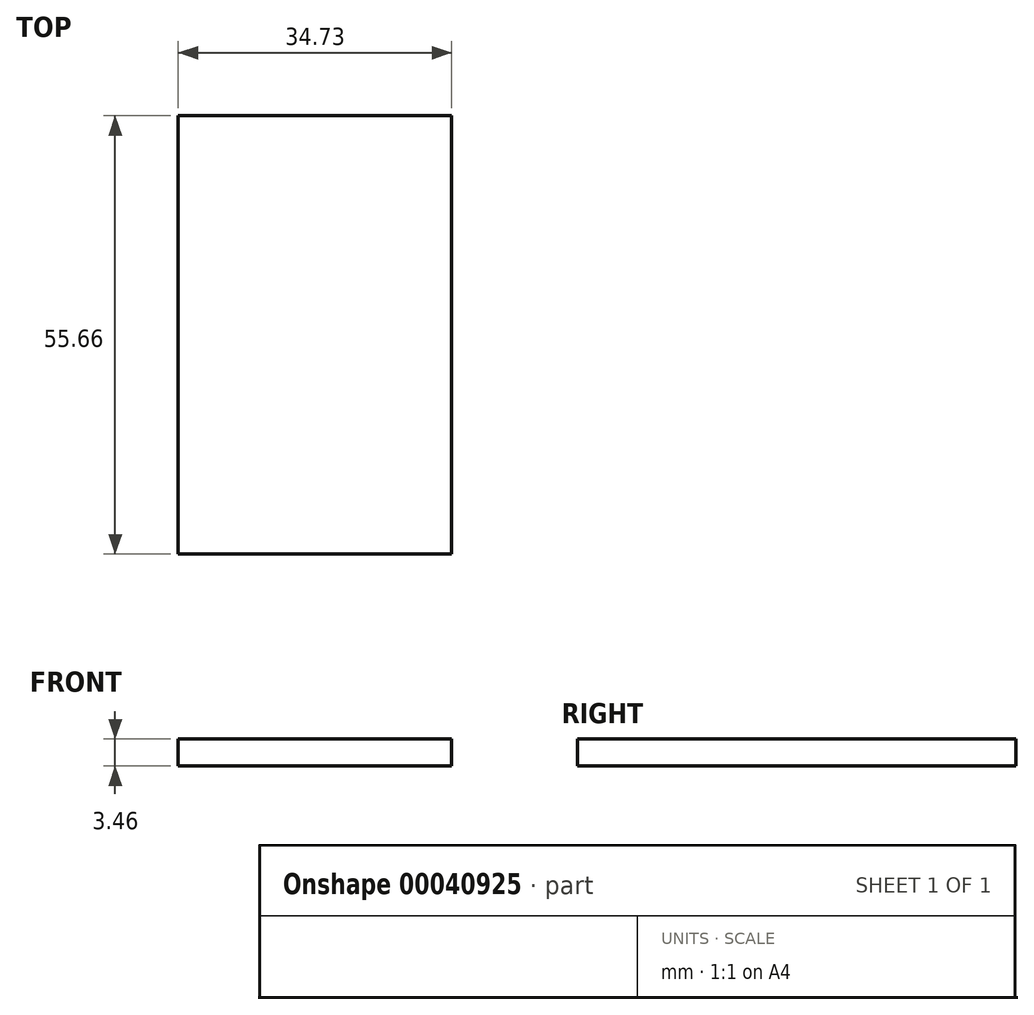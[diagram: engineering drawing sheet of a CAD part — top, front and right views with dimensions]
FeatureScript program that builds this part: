
annotation { "Feature Type Name" : "Feature", "Feature Type Description" : "" }
export const myFeature = defineFeature(function(context is Context, id is Id, definition is map)
    precondition{}
    {
        {
            var Q0;
            Q0=qCreatedBy(makeId("Top.planeOp"),FACE);
            var sketch = newSketch(context, id + "F0", { "sketchPlane" : qUnion([Q0])});
            skLineSegment(sketch, "E0.bottom", {"start": v(0, 0) * mm, "end": v(34.73, 0) * mm});
            skLineSegment(sketch, "E0.top", {"start": v(0, 55.66) * mm, "end": v(34.73, 55.66) * mm});
            skLineSegment(sketch, "E0.left", {"start": v(0, 0) * mm, "end": v(0, 55.66) * mm});
            skLineSegment(sketch, "E0.right", {"start": v(34.73, 0) * mm, "end": v(34.73, 55.66) * mm});
            skSolve(sketch);
        }
        {
            var Q0;
            Q0=makeQuery(id+"F0.imprint","IMPRINT",FACE,{"disambiguationData":[TD([[makeQuery(id+"F0.imprint","IMPRINT",EDGE,{"derivedFrom":sQuery(id+"F0.wireOp",EDGE,"E0.bottom")}),1.0]])]});
            extrude(context, id + "F1", {"entities" : qUnion([Q0]), "oppositeDirection" : true, "depth" : 3.46 * mm});
        }
        {
            var Q0;
            Q0=qCreatedBy(makeId("Top.planeOp"),FACE);
            var sketch = newSketch(context, id + "F2", { "sketchPlane" : qUnion([Q0])});
            skLineSegment(sketch, "E1.bottom", {"start": v(2.8, 53.49) * mm, "end": v(32.42, 53.49) * mm});
            skLineSegment(sketch, "E1.top", {"start": v(2.8, 39.32) * mm, "end": v(32.42, 39.32) * mm});
            skLineSegment(sketch, "E1.left", {"start": v(2.8, 53.49) * mm, "end": v(2.8, 39.32) * mm});
            skLineSegment(sketch, "E1.right", {"start": v(32.42, 53.49) * mm, "end": v(32.42, 39.32) * mm});
            skSolve(sketch);
        }
        {
            var Q0;
            Q0 = qSketchRegion(id + "F2", true);
            extrude(context, id + "F3", {"entities" : qUnion([Q0]), "operationType" : NewBodyOperationType.ADD, "oppositeDirection" : true, "depth" : 0.5 * mm});
        }
    });
